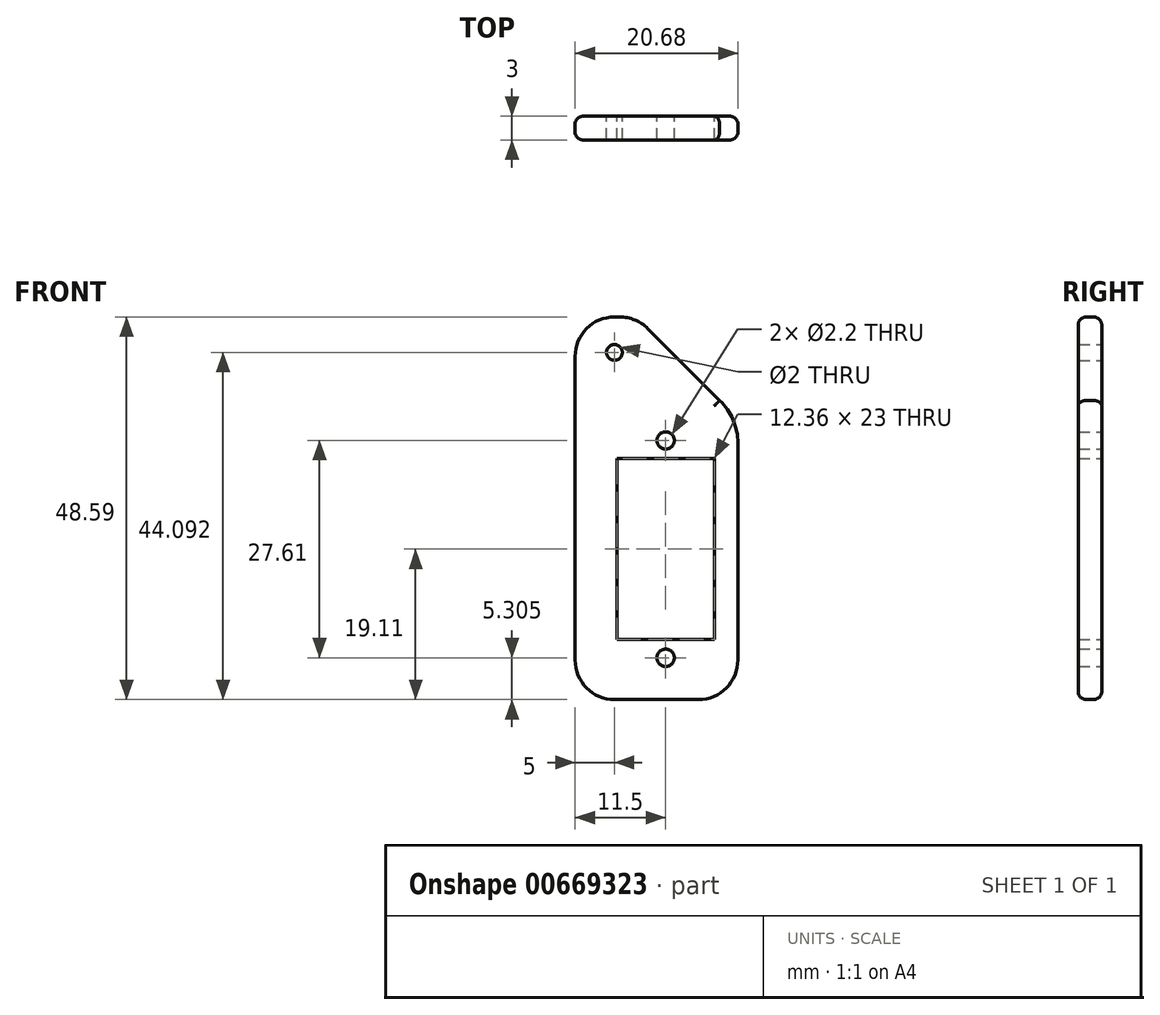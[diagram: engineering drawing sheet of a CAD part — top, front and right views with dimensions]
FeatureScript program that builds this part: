
annotation { "Feature Type Name" : "Feature", "Feature Type Description" : "" }
export const myFeature = defineFeature(function(context is Context, id is Id, definition is map)
    precondition{}
    {
        {
            var Q0;
            Q0=qCreatedBy(makeId("Front.planeOp"),FACE);
            var sketch = newSketch(context, id + "F0", { "sketchPlane" : qUnion([Q0])});
            skLineSegment(sketch, "E0.top", {"start": v(17.68, -22.43) * mm, "end": v(5.32, -22.43) * mm});
            skLineSegment(sketch, "E0.left", {"start": v(18.36, 12.56) * mm, "end": v(18.36, -22.43) * mm});
            skPoint(sketch, "E0.middle", {"position": v(0, 0) * mm});
            skLineSegment(sketch, "E1.bottom", {"start": v(5.32, -22.43) * mm, "end": v(17.68, -22.43) * mm});
            skLineSegment(sketch, "E1.top", {"start": v(5.32, 5.18) * mm, "end": v(17.68, 5.18) * mm});
            skLineSegment(sketch, "E1.left", {"start": v(5.32, -22.43) * mm, "end": v(5.32, 5.18) * mm});
            skLineSegment(sketch, "E1.right", {"start": v(17.68, -22.43) * mm, "end": v(17.68, 5.18) * mm});
            skLineSegment(sketch, "E2.bottom", {"start": v(5.32, 0) * mm, "end": v(17.68, 0) * mm});
            skLineSegment(sketch, "E2.top", {"start": v(5.32, -17.82) * mm, "end": v(17.68, -17.82) * mm});
            skLineSegment(sketch, "E2.left", {"start": v(5.32, 0) * mm, "end": v(5.32, -17.82) * mm});
            skLineSegment(sketch, "E2.right", {"start": v(17.68, 0) * mm, "end": v(17.68, -17.82) * mm});
            skLineSegment(sketch, "E3.bottom", {"start": v(17.68, 5.18) * mm, "end": v(5.32, 5.18) * mm});
            skLineSegment(sketch, "E3.top", {"start": v(17.68, 9.8) * mm, "end": v(5.32, 9.8) * mm});
            skLineSegment(sketch, "E3.left", {"start": v(17.68, 5.18) * mm, "end": v(17.68, 9.8) * mm});
            skLineSegment(sketch, "E3.right", {"start": v(5.32, 5.18) * mm, "end": v(5.32, 9.8) * mm});
            skLineSegment(sketch, "E4", {"start": v(5.32, 9.8) * mm, "end": v(17.68, 5.18) * mm, "construction": true});
            skLineSegment(sketch, "E5", {"start": v(5.32, -17.82) * mm, "end": v(17.68, -22.43) * mm, "construction": true});
            skCircle(sketch, "E6", {"center": v(11.5, 7.49) * mm, "radius": 1.1 * mm});
            skLineSegment(sketch, "E7.top", {"start": v(-18.36, -25.43) * mm, "end": v(18.36, -25.43) * mm});
            skLineSegment(sketch, "E7.right", {"start": v(18.36, -22.43) * mm, "end": v(18.36, -25.43) * mm});
            skLineSegment(sketch, "E8", {"start": v(0, 32.14) * mm, "end": v(0, 0) * mm, "construction": true});
            skLineSegment(sketch, "E9", {"start": v(-18.36, 0) * mm, "end": v(18.36, 0) * mm, "construction": true});
            skCircle(sketch, "E10", {"center": v(11.5, -20.12) * mm, "radius": 1.1 * mm});
            skLineSegment(sketch, "E11.bottom", {"start": v(0, -25.43) * mm, "end": v(18.36, -25.43) * mm});
            skLineSegment(sketch, "E12", {"start": v(-18.36, 12.56) * mm, "end": v(-7.75, 23.16) * mm});
            skLineSegment(sketch, "E13", {"start": v(7.75, 23.16) * mm, "end": v(18.36, 12.56) * mm});
            skLineSegment(sketch, "E14", {"start": v(-18.36, 12.56) * mm, "end": v(-18.36, 23.16) * mm, "construction": true});
            skLineSegment(sketch, "E15", {"start": v(18.36, 12.56) * mm, "end": v(18.36, 23.49) * mm, "construction": true});
            skCircle(sketch, "E16", {"center": v(-5, 18.66) * mm, "radius": 1 * mm});
            skCircle(sketch, "E17", {"center": v(5, 18.66) * mm, "radius": 1 * mm});
            skCircle(sketch, "E18", {"center": v(-11.5, -1) * mm, "radius": 1.3 * mm});
            skLineSegment(sketch, "E19", {"start": v(-7.75, 23.16) * mm, "end": v(7.75, 23.16) * mm});
            skCircle(sketch, "E20", {"center": v(11.5, -1) * mm, "radius": 6.18 * mm});
            skLineSegment(sketch, "E21", {"start": v(11.5, -1) * mm, "end": v(-6.79, -1) * mm, "construction": true});
            skLineSegment(sketch, "E22", {"start": v(-10.25, -1) * mm, "end": v(-10.25, 21.43) * mm, "construction": true});
            skLineSegment(sketch, "E23", {"start": v(18.36, 12.56) * mm, "end": v(20.68, 12.56) * mm});
            skLineSegment(sketch, "E24", {"start": v(20.68, 12.56) * mm, "end": v(20.68, -25.43) * mm});
            skLineSegment(sketch, "E25", {"start": v(-18.36, 12.56) * mm, "end": v(-20.68, 12.56) * mm});
            skLineSegment(sketch, "E26", {"start": v(18.36, -25.43) * mm, "end": v(20.68, -25.43) * mm});
            skLineSegment(sketch, "E27", {"start": v(0, 23.16) * mm, "end": v(0, -25.43) * mm});
            skPoint(sketch, "E11.right.end.orphan", {"position": v(18.36, -28.43) * mm});
            skPoint(sketch, "E28.orphan", {"position": v(20.68, -28.43) * mm});
            skSolve(sketch);
        }
        {
            var Q0;
            Q0=qSketchRegion(id+"F0",true);
            var Q1;
            {var subQ2=sQuery(id+"F0.wireOp",EDGE,"E2.top");Q1=makeQuery(id+"F0.imprint","IMPRINT",FACE,{"disambiguationData":[TD([[makeQuery(id+"F0.imprint","IMPRINT",EDGE,{"derivedFrom":subQ2}),-1.0]])]});}
            var Q2;
            Q2=makeQuery(id+"F0.imprint","IMPRINT",FACE,{"disambiguationData":[TD([[makeQuery(id+"F0.imprint","IMPRINT",EDGE,{"derivedFrom":sQuery(id+"F0.wireOp",EDGE,"E3.top")}),1.0]])]});
            var Q3;
            {var subQ0=sQuery(id+"F0.wireOp",EDGE,"E3.bottom");var subQ1=sQuery(id+"F0.wireOp",EDGE,"FkeFUImi-7huS-bPcJ-8ver-gJrOx2cKMFpE");var subQ2=makeQuery(id+"F0.imprint","INTERSECT",VERTEX,{"disambiguationData":[OD(0.0)],"derivedFrom":[subQ1,subQ0]});Q3=makeQuery(id+"F0.imprint","IMPRINT",FACE,{"disambiguationData":[TD([[makeQuery(id+"F0.imprint","IMPRINT",EDGE,{"disambiguationData":[TD([[subQ2,-1.0]])],"derivedFrom":subQ1}),1.0]])]});}
            extrude(context, id + "F1", {"entities" : qUnion([Q0, Q1, Q2, Q3]), "depth" : 3 * mm});
        }
        {
            var Q0;
            Q0=makeQuery(id+"F1.opExtrude","SWEPT_EDGE",EDGE,{"disambiguationData":[OSD([sQuery(id+"F0.wireOp",EDGE,"E23"),sQuery(id+"F0.wireOp",EDGE,"E24")])]});
            fillet(context, id + "F2", {"entities" : qUnion([Q0]), "radius" : 7.48 * mm, "tangentPropagation" : true, "allowEdgeOverflow" : false});
        }
        {
            var Q0;
            Q0=makeQuery(id+"F1.opExtrude","SWEPT_EDGE",EDGE,{"disambiguationData":[OSD([sQuery(id+"F0.wireOp",EDGE,"E13"),sQuery(id+"F0.wireOp",EDGE,"E19")])]});
            var Q1;
            Q1=makeQuery(id+"F1.opExtrude","SWEPT_EDGE",EDGE,{"disambiguationData":[OSD([sQuery(id+"F0.wireOp",EDGE,"E19"),sQuery(id+"F0.wireOp",EDGE,"E27")])]});
            var Q2;
            Q2=makeQuery(id+"F1.opExtrude","SWEPT_EDGE",EDGE,{"disambiguationData":[OSD([sQuery(id+"F0.wireOp",EDGE,"E11.bottom"),sQuery(id+"F0.wireOp",EDGE,"E27")])]});
            var Q3;
            Q3=makeQuery(id+"F1.opExtrude","SWEPT_EDGE",EDGE,{"disambiguationData":[OSD([sQuery(id+"F0.wireOp",EDGE,"E24"),sQuery(id+"F0.wireOp",EDGE,"E26")])]});
            fillet(context, id + "F3", {"entities" : qUnion([Q0, Q1, Q2, Q3]), "radius" : 5 * mm, "tangentPropagation" : true, "allowEdgeOverflow" : false});
        }
        {
            var Q0;
            Q0=makeQuery(id+"F1.opExtrude","SWEPT_BODY",BODY,{"disambiguationData":[OSD([sQuery(id+"F0.wireOp",EDGE,"E18")])]});
            deleteBodies(context, id + "F4", {"entities" : qUnion([Q0])});
        }
        {
            var Q0;
            Q0=makeQuery(id+"F1.opExtrude","SWEPT_BODY",BODY,{"disambiguationData":[OSD([sQuery(id+"F0.wireOp",EDGE,"E16")])]});
            deleteBodies(context, id + "F5", {"entities" : qUnion([Q0])});
        }
        {
            var Q0;
            Q0=makeQuery(id+"F1.opExtrude","CAP_EDGE",EDGE,{"disambiguationData":[OSD([sQuery(id+"F0.wireOp",EDGE,"E13")])],"isStart":true});
            var Q1;
            Q1=makeQuery(id+"F1.opExtrude","CAP_EDGE",EDGE,{"disambiguationData":[OSD([sQuery(id+"F0.wireOp",EDGE,"E27")])],"isStart":false});
            fillet(context, id + "F6", {"entities" : qUnion([Q0, Q1]), "radius" : 1 * mm, "tangentPropagation" : true, "allowEdgeOverflow" : false});
        }
    });
